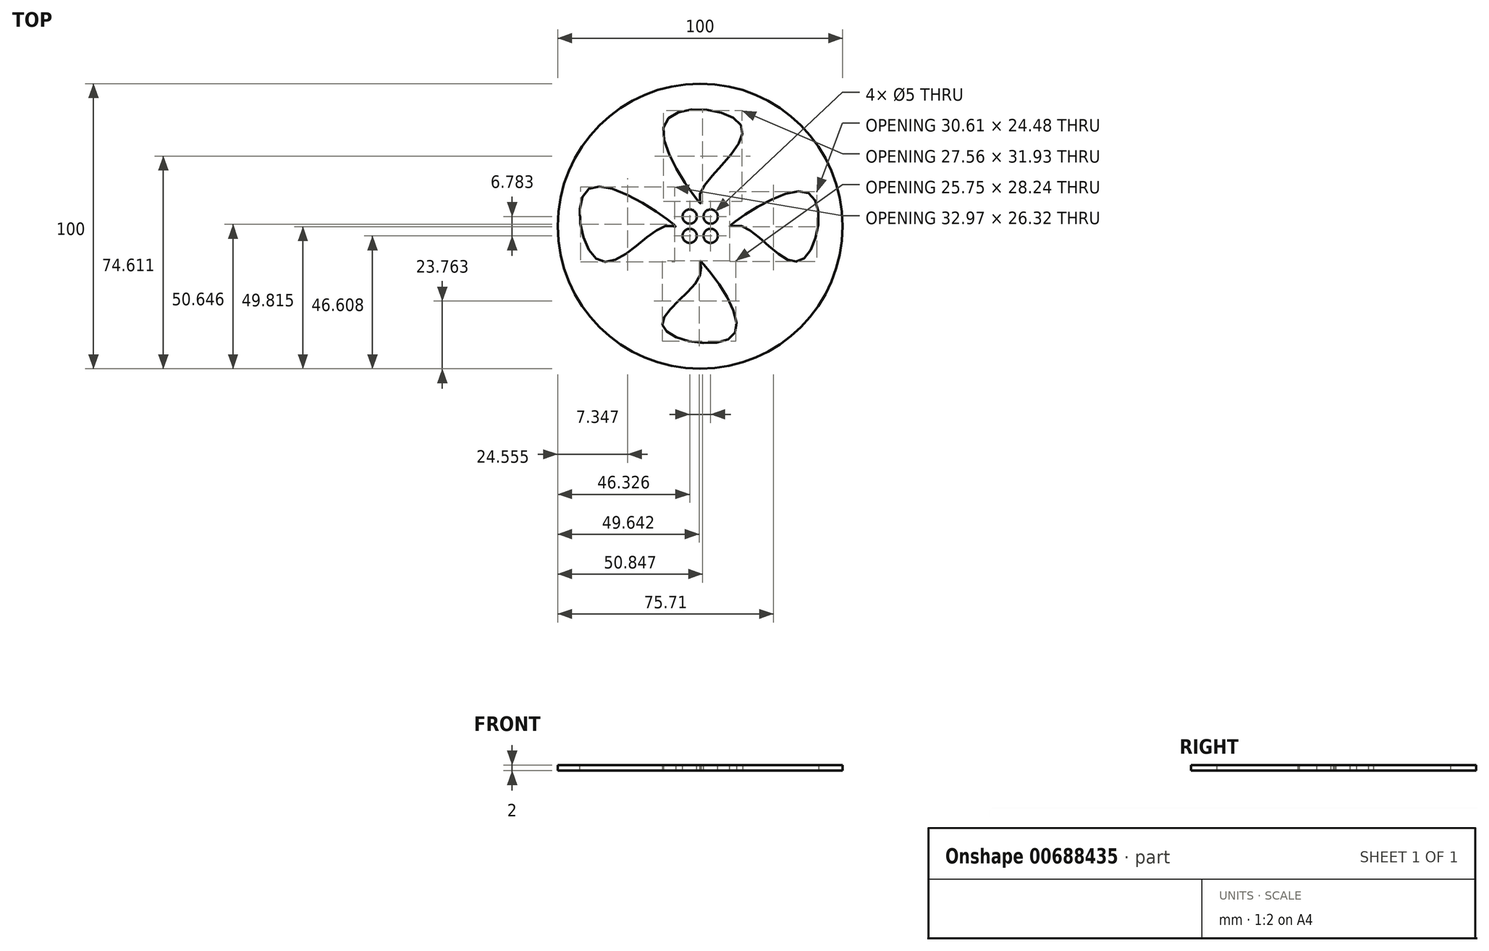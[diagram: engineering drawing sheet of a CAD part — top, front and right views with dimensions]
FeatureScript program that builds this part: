
annotation { "Feature Type Name" : "Feature", "Feature Type Description" : "" }
export const myFeature = defineFeature(function(context is Context, id is Id, definition is map)
    precondition{}
    {
        {
            var Q0;
            Q0=qCreatedBy(makeId("Top.planeOp"),FACE);
            var sketch = newSketch(context, id + "F0", { "sketchPlane" : qUnion([Q0])});
            skCircle(sketch, "E0", {"center": v(0, 0) * mm, "radius": 50 * mm});
            skSolve(sketch);
        }
        {
            var Q0;
            Q0=makeQuery(id+"F0.imprint","IMPRINT",FACE,{"disambiguationData":[TD([[makeQuery(id+"F0.imprint","IMPRINT",EDGE,{"derivedFrom":sQuery(id+"F0.wireOp",EDGE,"E0")}),1.0]])]});
            extrude(context, id + "F1", {"entities" : qUnion([Q0]), "depth" : 2 * mm, "offsetDistance" : 25 * mm});
        }
        {
            var Q0;
            Q0=makeQuery(id+"F1.opExtrude","CAP_FACE",FACE,{"disambiguationData":[OSD([sQuery(id+"F0.wireOp",EDGE,"E0")])],"isStart":false});
            var sketch = newSketch(context, id + "F2", { "sketchPlane" : qUnion([Q0])});
            skCircle(sketch, "E1", {"center": v(0, 0) * mm, "radius": 5 * mm});
            skCircle(sketch, "E2", {"center": v(3.67, -3.4) * mm, "radius": 2.5 * mm});
            skCircle(sketch, "E3", {"center": v(3.67, 3.4) * mm, "radius": 2.5 * mm});
            skCircle(sketch, "E4", {"center": v(-3.67, -3.4) * mm, "radius": 2.5 * mm});
            skCircle(sketch, "E5", {"center": v(-3.67, 3.4) * mm, "radius": 2.5 * mm});
            skSolve(sketch);
        }
        {
            var Q0;
            Q0=sQuery(id+"F2.wireOp",VERTEX,"E2.center");
            var Q1;
            Q1=sQuery(id+"F2.wireOp",VERTEX,"E3.center");
            var Q2;
            Q2=sQuery(id+"F2.wireOp",VERTEX,"E5.center");
            var Q3;
            Q3=sQuery(id+"F2.wireOp",VERTEX,"E4.center");
            var Q4;
            Q4=makeQuery(id+"F1.opExtrude","SWEPT_BODY",BODY,{"disambiguationData":[OSD([sQuery(id+"F0.wireOp",EDGE,"E0")])]});
            hole(context, id + "F3", {"style" : HoleStyle.SIMPLE, "endStyle" : HoleEndStyle.THROUGH, "holeDiameter" : 5 * mm, "majorDiameter" : 5 * mm, "isTappedThrough" : true, "tappedDepth" : 23.25 * mm, "tapClearance" : 3, "locations" : qUnion([Q0, Q1, Q2, Q3]), "scope" : qUnion([Q4])});
        }
        {
            var Q0;
            Q0=makeQuery(id+"F1.opExtrude","CAP_FACE",FACE,{"disambiguationData":[OSD([sQuery(id+"F0.wireOp",EDGE,"E0")])],"isStart":true});
            var sketch = newSketch(context, id + "F4", { "sketchPlane" : qUnion([Q0])});
            skFitSpline(sketch, "E6", {"points": [v(0, 17.16) * mm, v(-13.01, 35.28) * mm, v(12.24, 37.4) * mm, v(0, 12.15) * mm, v(0, 17.16) * mm]});
            skFitSpline(sketch, "E7", {"points": [v(14.55, 0) * mm, v(35.18, 12.15) * mm, v(38.07, -11.57) * mm, v(10.31, 0) * mm, v(14.55, 0) * mm]});
            skFitSpline(sketch, "E8", {"points": [v(0, -11.37) * mm, v(14.55, -34.9) * mm, v(-12.24, -36.44) * mm, v(0, -8.1) * mm, v(0, -11.37) * mm]});
            skFitSpline(sketch, "E9", {"points": [v(-12.24, 0) * mm, v(-35.18, 12.15) * mm, v(-38.65, -13.3) * mm, v(-8.58, 0) * mm, v(-12.24, 0) * mm]});
            skSolve(sketch);
        }
        {
            var Q0;
            Q0=makeQuery(id+"F4.imprint","IMPRINT",FACE,{"disambiguationData":[TD([[makeQuery(id+"F4.imprint","IMPRINT",EDGE,{"derivedFrom":sQuery(id+"F4.wireOp",EDGE,"E9")}),1.0]])]});
            extrude(context, id + "F5", {"entities" : qUnion([Q0]), "operationType" : NewBodyOperationType.REMOVE, "oppositeDirection" : true, "depth" : 2 * mm, "offsetDistance" : 25 * mm});
        }
        {
            var Q0;
            Q0=makeQuery(id+"F4.imprint","IMPRINT",FACE,{"disambiguationData":[TD([[makeQuery(id+"F4.imprint","IMPRINT",EDGE,{"derivedFrom":sQuery(id+"F4.wireOp",EDGE,"E6")}),-1.0]])]});
            var Q1;
            Q1=makeQuery(id+"F4.imprint","IMPRINT",FACE,{"disambiguationData":[TD([[makeQuery(id+"F4.imprint","IMPRINT",EDGE,{"derivedFrom":sQuery(id+"F4.wireOp",EDGE,"E7")}),-1.0]])]});
            var Q2;
            Q2=makeQuery(id+"F4.imprint","IMPRINT",FACE,{"disambiguationData":[TD([[makeQuery(id+"F4.imprint","IMPRINT",EDGE,{"derivedFrom":sQuery(id+"F4.wireOp",EDGE,"E8")}),-1.0]])]});
            extrude(context, id + "F6", {"entities" : qUnion([Q0, Q1, Q2]), "operationType" : NewBodyOperationType.REMOVE, "oppositeDirection" : true, "depth" : 2 * mm, "offsetDistance" : 25 * mm});
        }
    });
